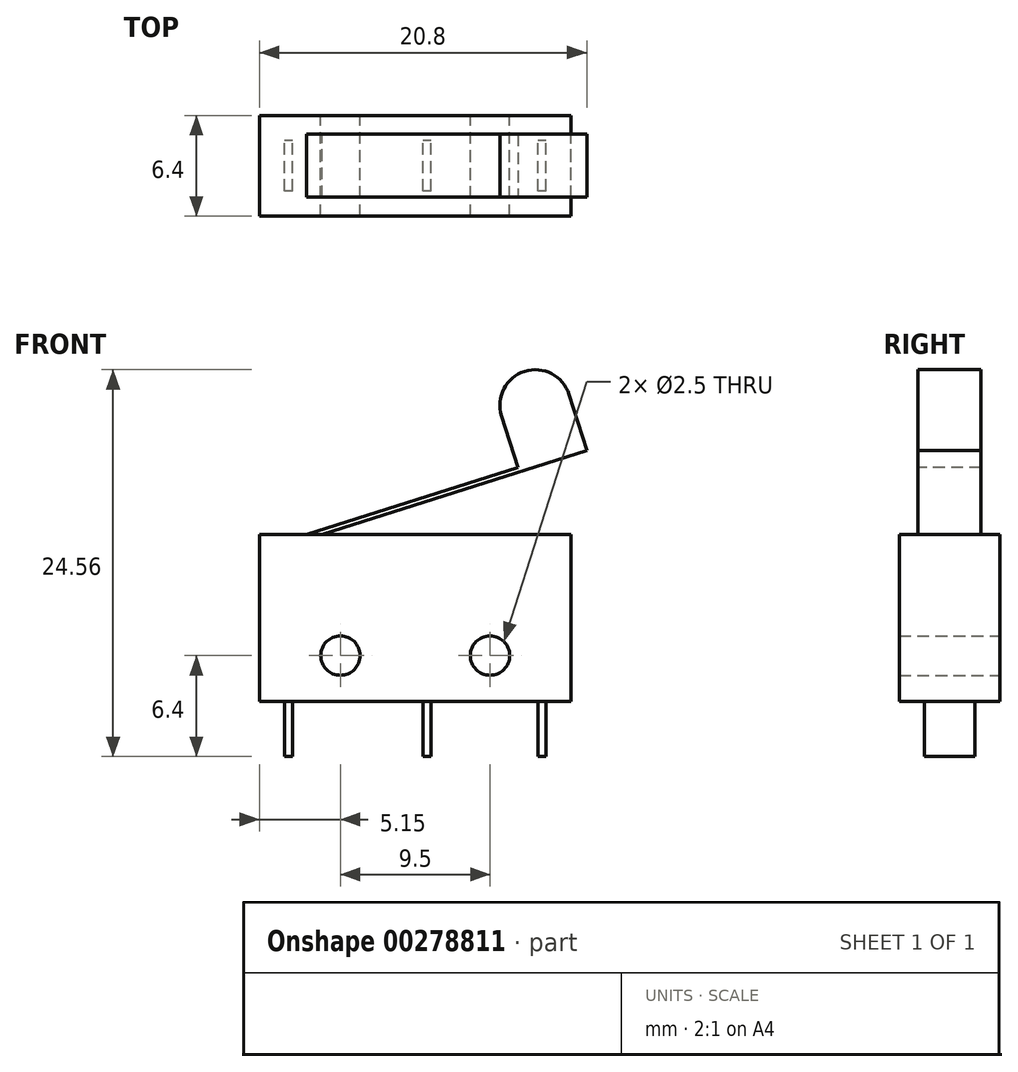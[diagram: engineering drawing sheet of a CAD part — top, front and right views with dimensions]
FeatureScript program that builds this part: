
annotation { "Feature Type Name" : "Feature", "Feature Type Description" : "" }
export const myFeature = defineFeature(function(context is Context, id is Id, definition is map)
    precondition{}
    {
        {
            var Q0;
            Q0=qCreatedBy(makeId("Front.planeOp"),FACE);
            var sketch = newSketch(context, id + "F0", { "sketchPlane" : qUnion([Q0])});
            skLineSegment(sketch, "E0.bottom", {"start": v(9.9, 5.3) * mm, "end": v(-9.9, 5.3) * mm});
            skLineSegment(sketch, "E0.top", {"start": v(9.9, -5.3) * mm, "end": v(-9.9, -5.3) * mm});
            skLineSegment(sketch, "E0.left", {"start": v(9.9, 5.3) * mm, "end": v(9.9, -5.3) * mm});
            skLineSegment(sketch, "E0.right", {"start": v(-9.9, 5.3) * mm, "end": v(-9.9, -5.3) * mm});
            skPoint(sketch, "E0.middle", {"position": v(0, 0) * mm});
            skLineSegment(sketch, "E1", {"start": v(0, 0) * mm, "end": v(0, -5.3) * mm, "construction": true});
            skCircle(sketch, "E2", {"center": v(-4.75, -2.4) * mm, "radius": 1.25 * mm});
            skCircle(sketch, "E3.MirrorC", {"center": v(4.75, -2.4) * mm, "radius": 1.25 * mm});
            skSolve(sketch);
        }
        {
            var Q0;
            Q0 = qSketchRegion(id + "F0", true);
            extrude(context, id + "F1", {"entities" : qUnion([Q0]), "endBound" : BoundingType.SYMMETRIC, "depth" : 6.4 * mm});
        }
        {
            var Q0;
            Q0=makeQuery(id+"F1.opExtrude","SWEPT_FACE",FACE,{"disambiguationData":[OSD([sQuery(id+"F0.wireOp",EDGE,"E0.top")])]});
            var sketch = newSketch(context, id + "F2", { "sketchPlane" : qUnion([Q0])});
            skLineSegment(sketch, "E4", {"start": v(-9.9, 0) * mm, "end": v(9.9, 0) * mm, "construction": true});
            skLineSegment(sketch, "E5.bottom", {"start": v(-7.8, 1.6) * mm, "end": v(-8.3, 1.6) * mm});
            skLineSegment(sketch, "E5.top", {"start": v(-7.8, -1.6) * mm, "end": v(-8.3, -1.6) * mm});
            skLineSegment(sketch, "E5.left", {"start": v(-7.8, 1.6) * mm, "end": v(-7.8, -1.6) * mm});
            skLineSegment(sketch, "E5.right", {"start": v(-8.3, 1.6) * mm, "end": v(-8.3, -1.6) * mm});
            skPoint(sketch, "E5.middle", {"position": v(-8.05, 0) * mm});
            skLineSegment(sketch, "E6.bottom", {"start": v(1, 1.6) * mm, "end": v(0.5, 1.6) * mm});
            skLineSegment(sketch, "E6.top", {"start": v(1, -1.6) * mm, "end": v(0.5, -1.6) * mm});
            skLineSegment(sketch, "E6.left", {"start": v(1, 1.6) * mm, "end": v(1, -1.6) * mm});
            skLineSegment(sketch, "E6.right", {"start": v(0.5, 1.6) * mm, "end": v(0.5, -1.6) * mm});
            skPoint(sketch, "E6.middle", {"position": v(0.75, 0) * mm});
            skLineSegment(sketch, "E7.bottom", {"start": v(8.3, 1.6) * mm, "end": v(7.8, 1.6) * mm});
            skLineSegment(sketch, "E7.top", {"start": v(8.3, -1.6) * mm, "end": v(7.8, -1.6) * mm});
            skLineSegment(sketch, "E7.left", {"start": v(8.3, 1.6) * mm, "end": v(8.3, -1.6) * mm});
            skLineSegment(sketch, "E7.right", {"start": v(7.8, 1.6) * mm, "end": v(7.8, -1.6) * mm});
            skPoint(sketch, "E7.middle", {"position": v(8.05, 0) * mm});
            skSolve(sketch);
        }
        {
            var Q0;
            Q0 = qSketchRegion(id + "F2", true);
            extrude(context, id + "F3", {"entities" : qUnion([Q0]), "operationType" : NewBodyOperationType.ADD, "depth" : 3.5 * mm});
        }
        {
            var Q0;
            Q0=qCreatedBy(makeId("Front.planeOp"),FACE);
            var sketch = newSketch(context, id + "F4", { "sketchPlane" : qUnion([Q0])});
            skLineSegment(sketch, "E8.0", {"start": v(9.9, 5.3) * mm, "end": v(-9.9, 5.3) * mm, "construction": true});
            skLineSegment(sketch, "E9", {"start": v(-6.9, 5.3) * mm, "end": v(10.8, 10.9) * mm});
            skLineSegment(sketch, "E10", {"start": v(-6.9, 5.3) * mm, "end": v(-5.9, 5.3) * mm});
            skLineSegment(sketch, "E11", {"start": v(-5.9, 5.3) * mm, "end": v(10.9, 10.61) * mm});
            skLineSegment(sketch, "E12", {"start": v(10.9, 10.61) * mm, "end": v(10.8, 10.9) * mm});
            skSolve(sketch);
        }
        {
            var Q0;
            Q0 = qSketchRegion(id + "F4", true);
            extrude(context, id + "F5", {"entities" : qUnion([Q0]), "operationType" : NewBodyOperationType.ADD, "endBound" : BoundingType.SYMMETRIC, "depth" : 4 * mm});
        }
        {
            var Q0;
            Q0=makeQuery(id+"F5.opExtrude","CAP_FACE",FACE,{"disambiguationData":[OSD([sQuery(id+"F4.wireOp",EDGE,"E9"),sQuery(id+"F4.wireOp",EDGE,"E10"),sQuery(id+"F4.wireOp",EDGE,"E11"),sQuery(id+"F4.wireOp",EDGE,"E12")])],"isStart":false});
            var sketch = newSketch(context, id + "F6", { "sketchPlane" : qUnion([Q0])});
            skLineSegment(sketch, "E13", {"start": v(10.8, 10.9) * mm, "end": v(9.77, 14.19) * mm});
            skLineSegment(sketch, "E14", {"start": v(10.8, 10.9) * mm, "end": v(6.52, 9.54) * mm});
            skLineSegment(sketch, "E15", {"start": v(6.52, 9.54) * mm, "end": v(5.48, 12.83) * mm});
            skArc(sketch, "E16", {"start": v(9.77, 14.19) * mm, "mid": v(6.95, 15.66) * mm, "end": v(5.48, 12.83) * mm});
            skPoint(sketch, "E17", {"position": v(6.95, 15.66) * mm});
            skSolve(sketch);
        }
        {
            var Q0;
            Q0 = qSketchRegion(id + "F6", true);
            var Q1;
            Q1=makeQuery(id+"F5.opExtrude","CAP_FACE",FACE,{"disambiguationData":[OSD([sQuery(id+"F4.wireOp",EDGE,"E9"),sQuery(id+"F4.wireOp",EDGE,"E10"),sQuery(id+"F4.wireOp",EDGE,"E11"),sQuery(id+"F4.wireOp",EDGE,"E12")])],"isStart":true});
            extrude(context, id + "F7", {"entities" : qUnion([Q0]), "operationType" : NewBodyOperationType.ADD, "endBound" : BoundingType.UP_TO_SURFACE, "oppositeDirection" : true, "endBoundEntityFace" : qUnion([Q1]), "depth" : 25 * mm});
        }
    });
